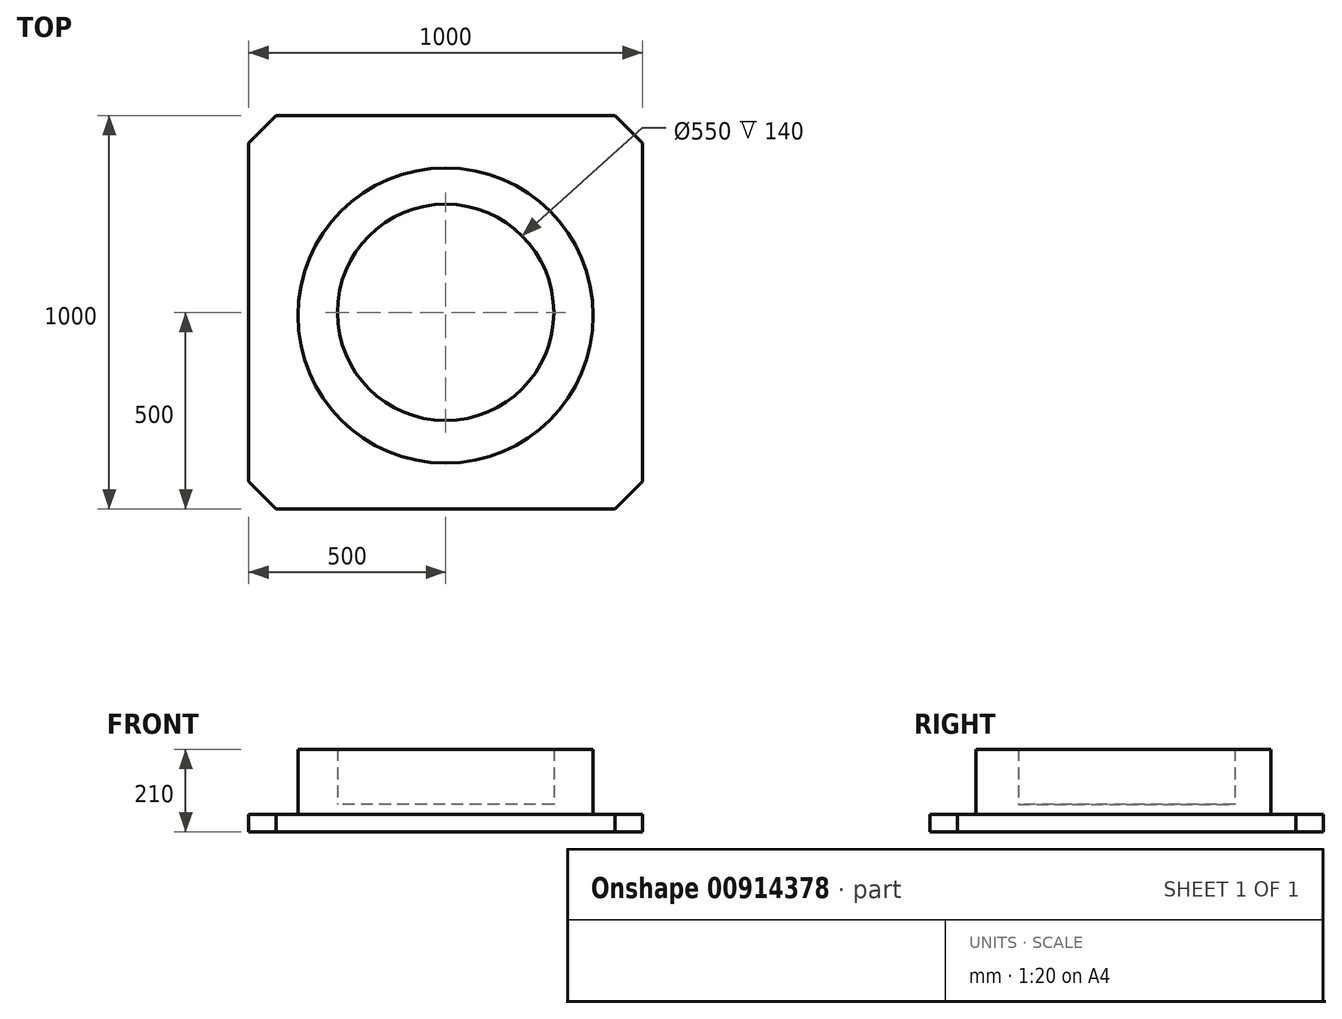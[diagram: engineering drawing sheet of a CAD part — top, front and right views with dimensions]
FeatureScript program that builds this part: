
annotation { "Feature Type Name" : "Feature", "Feature Type Description" : "" }
export const myFeature = defineFeature(function(context is Context, id is Id, definition is map)
    precondition{}
    {
        {
            var Q0;
            Q0=qCreatedBy(makeId("Top.planeOp"),FACE);
            var sketch = newSketch(context, id + "F0", { "sketchPlane" : qUnion([Q0])});
            skLineSegment(sketch, "E0.bottom", {"start": v(430, 500) * mm, "end": v(-430, 500) * mm});
            skLineSegment(sketch, "E0.top", {"start": v(430, -500) * mm, "end": v(-430, -500) * mm});
            skLineSegment(sketch, "E0.left", {"start": v(500, 430) * mm, "end": v(500, -430) * mm});
            skLineSegment(sketch, "E0.right", {"start": v(-500, 430) * mm, "end": v(-500, -430) * mm});
            skPoint(sketch, "E0.middle", {"position": v(0, 0) * mm});
            skLineSegment(sketch, "E1", {"start": v(-500, 430) * mm, "end": v(-430, 500) * mm});
            skLineSegment(sketch, "E2", {"start": v(430, 500) * mm, "end": v(500, 430) * mm});
            skLineSegment(sketch, "E3", {"start": v(-500, -430) * mm, "end": v(-430, -500) * mm});
            skLineSegment(sketch, "E4", {"start": v(430, -500) * mm, "end": v(500, -430) * mm});
            skPoint(sketch, "E5.orphan", {"position": v(-500, 500) * mm});
            skPoint(sketch, "E6.orphan", {"position": v(500, 500) * mm});
            skPoint(sketch, "E7.orphan", {"position": v(500, -500) * mm});
            skPoint(sketch, "E8.orphan", {"position": v(-500, -500) * mm});
            skSolve(sketch);
        }
        {
            var Q0;
            Q0 = qSketchRegion(id + "F0", true);
            extrude(context, id + "F1", {"entities" : qUnion([Q0]), "depth" : 45 * mm, "offsetDistance" : 25 * mm});
        }
        {
            var Q0;
            Q0=makeQuery(id+"F1.opExtrude","CAP_FACE",FACE,{"disambiguationData":[OSD([sQuery(id+"F0.wireOp",EDGE,"E0.bottom"),sQuery(id+"F0.wireOp",EDGE,"E0.top"),sQuery(id+"F0.wireOp",EDGE,"E0.left"),sQuery(id+"F0.wireOp",EDGE,"E0.right"),sQuery(id+"F0.wireOp",EDGE,"E1"),sQuery(id+"F0.wireOp",EDGE,"E2"),sQuery(id+"F0.wireOp",EDGE,"E3"),sQuery(id+"F0.wireOp",EDGE,"E4")])],"isStart":false});
            var sketch = newSketch(context, id + "F2", { "sketchPlane" : qUnion([Q0])});
            skCircle(sketch, "E9", {"center": v(0, -8.12) * mm, "radius": 375 * mm});
            skSolve(sketch);
        }
        {
            var Q0;
            Q0=makeQuery(id+"F2.imprint","IMPRINT",FACE,{"disambiguationData":[TD([[makeQuery(id+"F2.imprint","IMPRINT",EDGE,{"derivedFrom":sQuery(id+"F2.wireOp",EDGE,"E9")}),1.0]])]});
            extrude(context, id + "F3", {"entities" : qUnion([Q0]), "operationType" : NewBodyOperationType.ADD, "depth" : 25 * mm, "offsetDistance" : 25 * mm});
        }
        {
            var Q0;
            Q0=makeQuery(id+"F3.opExtrude","CAP_FACE",FACE,{"disambiguationData":[OSD([sQuery(id+"F2.wireOp",EDGE,"E9")])],"isStart":false});
            var sketch = newSketch(context, id + "F4", { "sketchPlane" : qUnion([Q0])});
            skCircle(sketch, "E10", {"center": v(0, 0) * mm, "radius": 275 * mm});
            skSolve(sketch);
        }
        {
            var Q0;
            Q0=makeQuery(id+"F4.imprint","IMPRINT",FACE,{"disambiguationData":[TD([[makeQuery(id+"F4.imprint","IMPRINT",EDGE,{"derivedFrom":sQuery(id+"F4.wireOp",EDGE,"E10")}),-1.0]])]});
            extrude(context, id + "F5", {"entities" : qUnion([Q0]), "operationType" : NewBodyOperationType.ADD, "depth" : 140 * mm, "offsetDistance" : 25 * mm});
        }
    });
